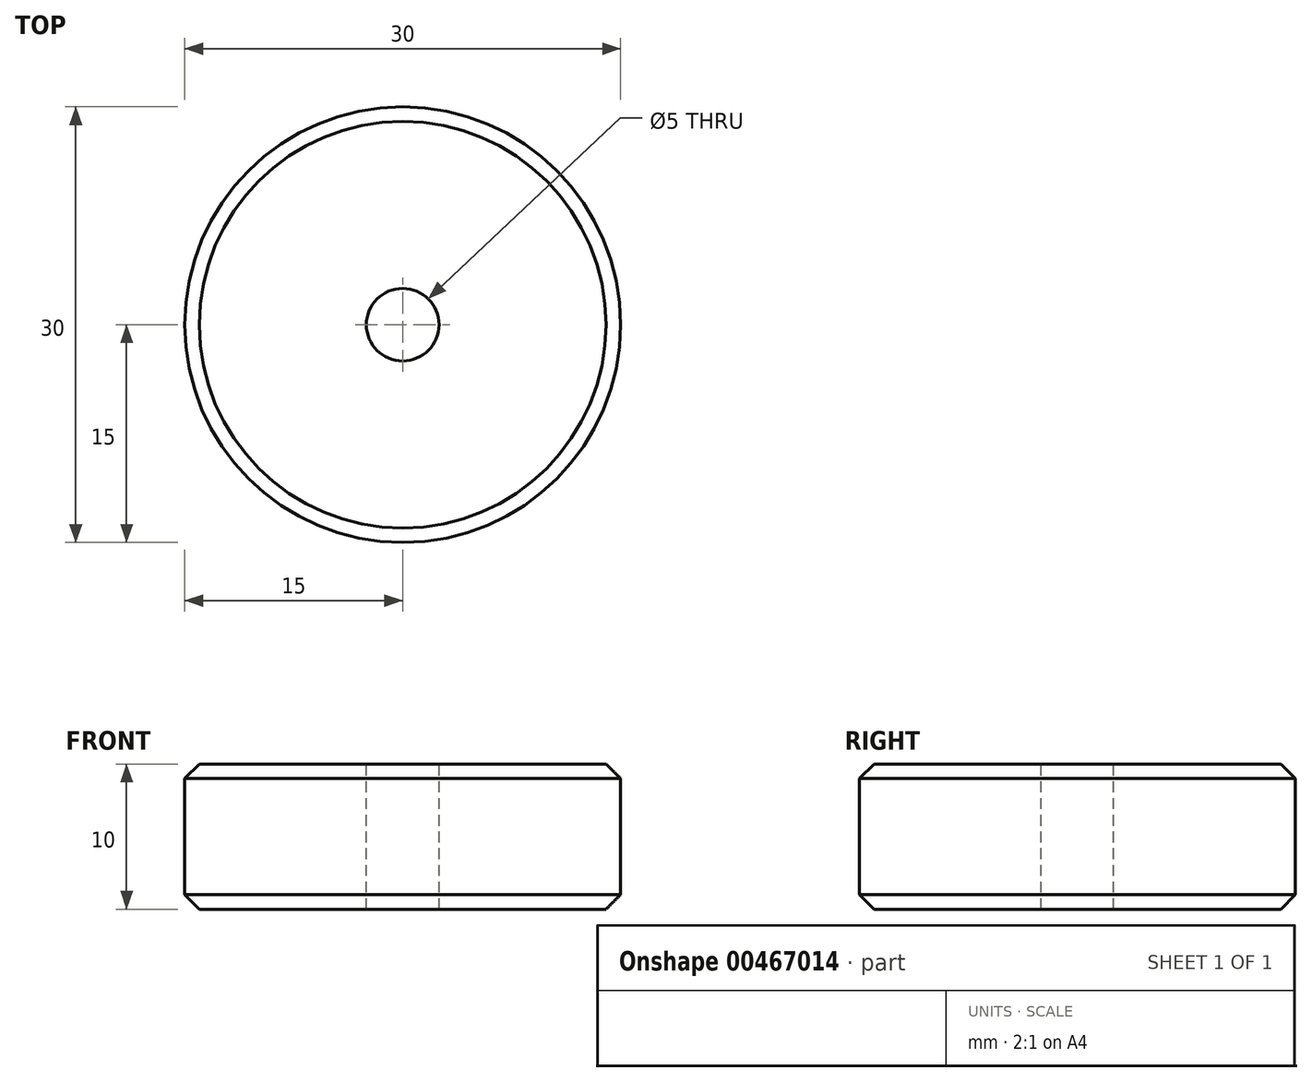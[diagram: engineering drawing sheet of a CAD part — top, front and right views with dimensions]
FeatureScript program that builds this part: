
annotation { "Feature Type Name" : "Feature", "Feature Type Description" : "" }
export const myFeature = defineFeature(function(context is Context, id is Id, definition is map)
    precondition{}
    {
        {
            var Q0;
            Q0=qCreatedBy(makeId("Top.planeOp"),FACE);
            var sketch = newSketch(context, id + "F0", { "sketchPlane" : qUnion([Q0])});
            skCircle(sketch, "E0", {"center": v(0, 0) * mm, "radius": 15 * mm});
            skSolve(sketch);
        }
        {
            var Q0;
            Q0=makeQuery(id+"F0.imprint","IMPRINT",FACE,{"disambiguationData":[TD([[makeQuery(id+"F0.imprint","IMPRINT",EDGE,{"derivedFrom":sQuery(id+"F0.wireOp",EDGE,"E0")}),1.0]])]});
            extrude(context, id + "F1", {"entities" : qUnion([Q0]), "depth" : 10 * mm});
        }
        {
            var Q0;
            Q0=makeQuery(id+"F1.opExtrude","CAP_EDGE",EDGE,{"disambiguationData":[OSD([sQuery(id+"F0.wireOp",EDGE,"E0")])],"isStart":false});
            var Q1;
            Q1=makeQuery(id+"F1.opExtrude","CAP_EDGE",EDGE,{"disambiguationData":[OSD([sQuery(id+"F0.wireOp",EDGE,"E0")])],"isStart":true});
            chamfer(context, id + "F2", {"entities" : qUnion([Q0, Q1]), "width" : 1 * mm, "tangentPropagation" : true});
        }
        {
            var Q0;
            Q0=makeQuery(id+"F1.opExtrude","CAP_FACE",FACE,{"disambiguationData":[OSD([sQuery(id+"F0.wireOp",EDGE,"E0")])],"isStart":false});
            var sketch = newSketch(context, id + "F3", { "sketchPlane" : qUnion([Q0])});
            skPoint(sketch, "E1", {"position": v(0, 0) * mm});
            skSolve(sketch);
        }
        {
            var Q0;
            Q0=sQuery(id+"F3.wireOp",VERTEX,"E1");
            var Q1;
            Q1=makeQuery(id+"F1.opExtrude","SWEPT_BODY",BODY,{"disambiguationData":[OSD([sQuery(id+"F0.wireOp",EDGE,"E0")])]});
            hole(context, id + "F4", {"style" : HoleStyle.SIMPLE, "endStyle" : HoleEndStyle.THROUGH, "holeDiameter" : 5 * mm, "isTappedThrough" : true, "tappedDepth" : 12 * mm, "tapClearance" : 3, "locations" : qUnion([Q0]), "scope" : qUnion([Q1]), "majorDiameter" : 5 * mm});
        }
    });
